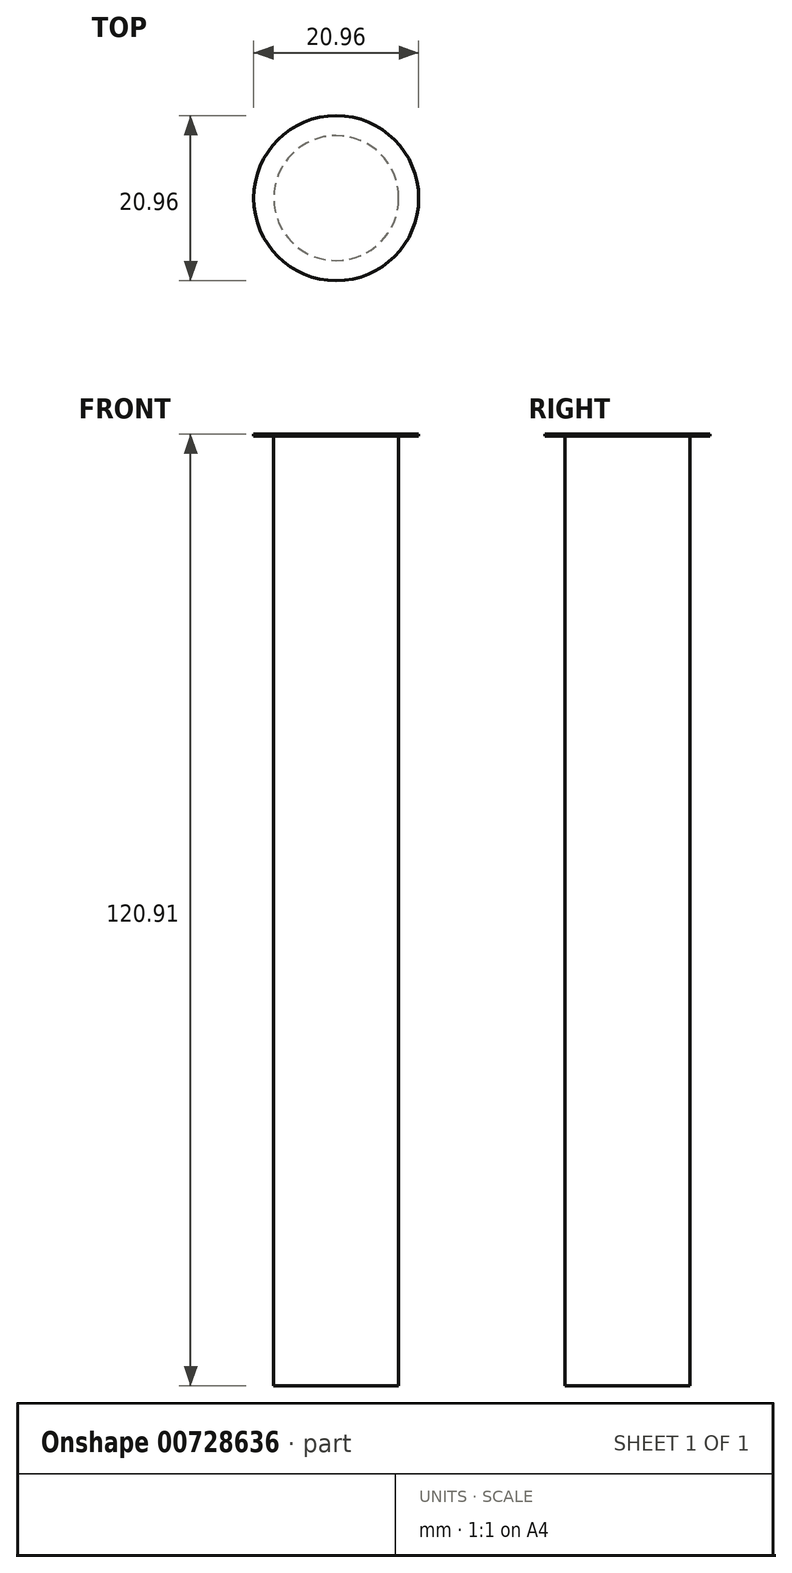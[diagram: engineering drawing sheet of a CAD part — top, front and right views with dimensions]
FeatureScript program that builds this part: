
annotation { "Feature Type Name" : "Feature", "Feature Type Description" : "" }
export const myFeature = defineFeature(function(context is Context, id is Id, definition is map)
    precondition{}
    {
        {
            assignVariable(context, id + "F0", {"name" : "head_thickness", "anyValue" : .25});
        }
        {
            var Q0;
            Q0=qCreatedBy(makeId("Top.planeOp"),FACE);
            var sketch = newSketch(context, id + "F1", { "sketchPlane" : qUnion([Q0])});
            skCircle(sketch, "E0", {"center": v(0, 0) * mm, "radius": 7.94 * mm});
            skSolve(sketch);
        }
        {
            var Q0;
            Q0=qSketchRegion(id+"F1",true);
            extrude(context, id + "F2", {"entities" : qUnion([Q0]), "endBound" : BoundingType.SYMMETRIC, "depth" : 120.65 * mm, "offsetDistance" : 25.4 * mm});
        }
        {
            var Q0;
            Q0=makeQuery(id+"F2.opExtrude","CAP_FACE",FACE,{"disambiguationData":[OSD([sQuery(id+"F1.wireOp",EDGE,"E0")])],"isStart":false});
            var sketch = newSketch(context, id + "F3", { "sketchPlane" : qUnion([Q0])});
            skCircle(sketch, "E1", {"center": v(0, 0) * mm, "radius": 10.48 * mm});
            skSolve(sketch);
        }
        {
            var Q0;
            Q0=qSketchRegion(id+"F3",true);
            extrude(context, id + "F4", {"entities" : qUnion([Q0]), "operationType" : NewBodyOperationType.ADD, "depth" : (getVariable(context, 'head_thickness')) * mm, "offsetDistance" : 25.4 * mm});
        }
    });
